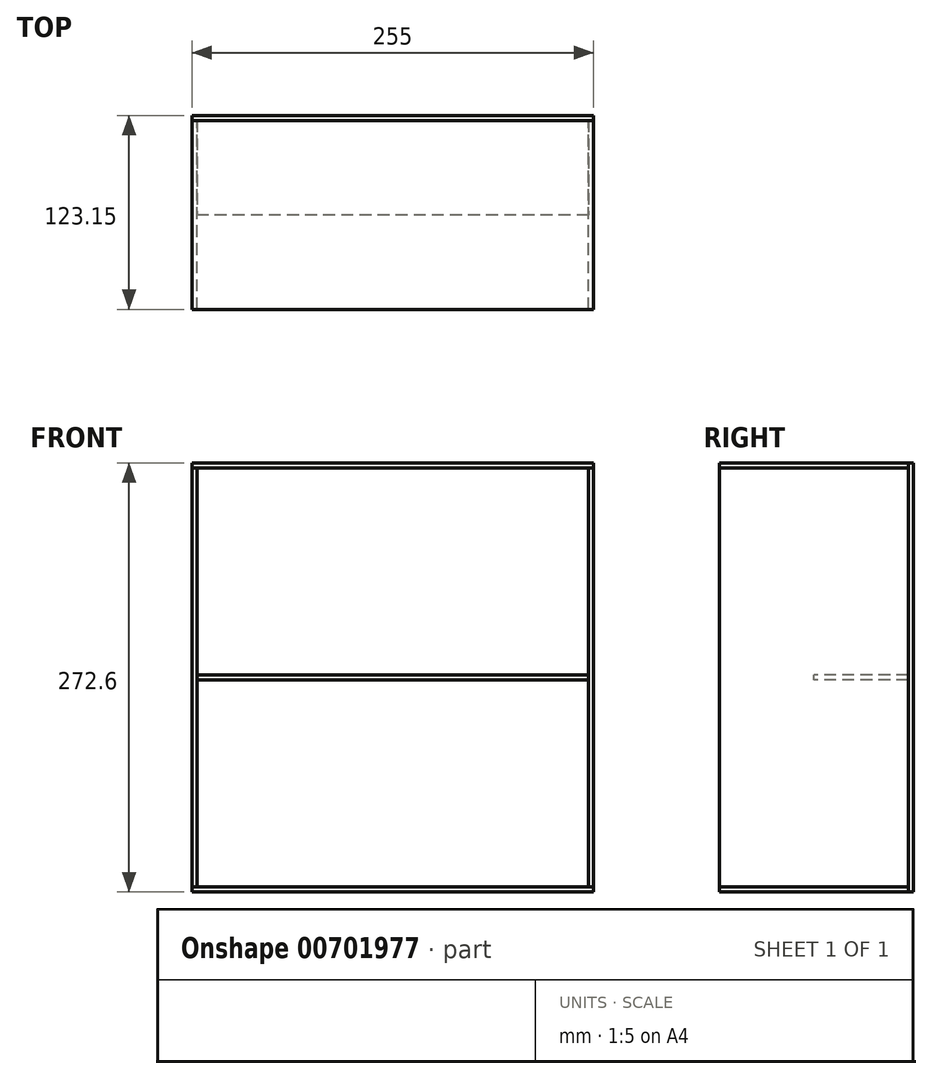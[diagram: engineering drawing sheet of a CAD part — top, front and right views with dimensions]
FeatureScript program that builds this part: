
annotation { "Feature Type Name" : "Feature", "Feature Type Description" : "" }
export const myFeature = defineFeature(function(context is Context, id is Id, definition is map)
    precondition{}
    {
        {
            assignVariable(context, id + "F0", {"name" : "x", "anyValue" : 3.15});
        }
        {
            var Q0;
            Q0=qCreatedBy(makeId("Top.planeOp"),FACE);
            var sketch = newSketch(context, id + "F1", { "sketchPlane" : qUnion([Q0])});
            skLineSegment(sketch, "E0.bottom", {"start": v(0, 0) * mm, "end": v(255, 0) * mm});
            skLineSegment(sketch, "E0.top", {"start": v(0, 120) * mm, "end": v(255, 120) * mm});
            skLineSegment(sketch, "E0.left", {"start": v(0, 0) * mm, "end": v(0, 120) * mm});
            skLineSegment(sketch, "E0.right", {"start": v(255, 0) * mm, "end": v(255, 120) * mm});
            skSolve(sketch);
        }
        {
            var Q0;
            Q0=qSketchRegion(id+"F1",true);
            extrude(context, id + "F2", {"entities" : qUnion([Q0]), "depth" : (getVariable(context, 'x')) * mm, "offsetDistance" : 25 * mm});
        }
        {
            var Q0;
            Q0=makeQuery(id+"F2.opExtrude","SWEPT_FACE",FACE,{"disambiguationData":[OSD([sQuery(id+"F1.wireOp",EDGE,"E0.left")])]});
            var sketch = newSketch(context, id + "F3", { "sketchPlane" : qUnion([Q0])});
            skLineSegment(sketch, "E1.top", {"start": v(0, 269.45) * mm, "end": v(-120, 269.45) * mm});
            skLineSegment(sketch, "E1.left", {"start": v(0, 3.15) * mm, "end": v(0, 269.45) * mm});
            skLineSegment(sketch, "E2", {"start": v(0, 3.15) * mm, "end": v(-120, 3.15) * mm});
            skLineSegment(sketch, "E3", {"start": v(-120, 3.15) * mm, "end": v(-120, 269.45) * mm});
            skSolve(sketch);
        }
        {
            var Q0;
            Q0=qSketchRegion(id+"F3",true);
            extrude(context, id + "F4", {"entities" : qUnion([Q0]), "oppositeDirection" : true, "depth" : (getVariable(context, 'x')) * mm, "offsetDistance" : 25 * mm});
        }
        {
            var Q0;
            Q0=makeQuery(id+"FVTuVMvbx6C6lcW_2.boolean.opBoolean","MERGE",FACE,{"derivedFrom":[makeQuery(id+"F4.opExtrude","SWEPT_FACE",FACE,{"disambiguationData":[OSD([sQuery(id+"F3.wireOp",EDGE,"E1.left")])]}),makeQuery(id+"FVTuVMvbx6C6lcW_2.opExtrude","SWEPT_FACE",FACE,{"disambiguationData":[OSD([sQuery(id+"F9WBSx8lvzqTq6O_2.wireOp",EDGE,"DdJYWYcg-8VXy-0sGO-iMAo-MInbchsGbsPU")])]})]});
            var sketch = newSketch(context, id + "F5", { "sketchPlane" : qUnion([Q0])});
            skLineSegment(sketch, "E4.bottom", {"start": v(3.15, 137.88) * mm, "end": v(251.85, 137.88) * mm});
            skLineSegment(sketch, "E4.top", {"start": v(3.15, 134.73) * mm, "end": v(251.85, 134.73) * mm});
            skLineSegment(sketch, "E4.right", {"start": v(251.85, 137.88) * mm, "end": v(251.85, 134.73) * mm});
            skLineSegment(sketch, "E5", {"start": v(251.85, 3.15) * mm, "end": v(251.85, 134.73) * mm, "construction": true});
            skLineSegment(sketch, "E6", {"start": v(3.15, 134.73) * mm, "end": v(3.15, 137.88) * mm});
            skPoint(sketch, "E7", {"position": v(3.15, 136.3) * mm});
            skSolve(sketch);
        }
        {
            var Q0;
            Q0=qSketchRegion(id+"F5",true);
            var Q1;
            Q1=makeQuery(id+"F4.opExtrude","SWEPT_FACE",FACE,{"disambiguationData":[OSD([sQuery(id+"F3.wireOp",EDGE,"E3")])]});
            extrude(context, id + "F6", {"entities" : qUnion([Q0]), "endBound" : BoundingType.UP_TO_SURFACE, "oppositeDirection" : true, "depth" : 25 * mm, "endBoundEntityFace" : qUnion([Q1]), "offsetDistance" : 25 * mm});
        }
        {
            var Q0;
            Q0=makeQuery(id+"F2.opExtrude","SWEPT_BODY",BODY,{"disambiguationData":[OSD([sQuery(id+"F1.wireOp",EDGE,"E0.bottom"),sQuery(id+"F1.wireOp",EDGE,"E0.top"),sQuery(id+"F1.wireOp",EDGE,"E0.left"),sQuery(id+"F1.wireOp",EDGE,"E0.right")])]});
            transform(context, id + "F7", {"entities" : qUnion([Q0]), "transformType" : TransformType.TRANSLATION_3D, "dx" : 0 * mm, "dy" : 0 * mm, "dz" : (266.3 + 3.15) * mm, "makeCopy" : true});
        }
        {
            var Q0;
            Q0=makeQuery(id+"F4.opExtrude","SWEPT_BODY",BODY,{"disambiguationData":[OSD([sQuery(id+"F3.wireOp",EDGE,"E1.top"),sQuery(id+"F3.wireOp",EDGE,"E1.left"),sQuery(id+"F3.wireOp",EDGE,"E2"),sQuery(id+"F3.wireOp",EDGE,"E3")])]});
            transform(context, id + "F8", {"entities" : qUnion([Q0]), "transformType" : TransformType.TRANSLATION_3D, "dx" : (263.7 + 3.15 - 15) * mm, "dy" : 0 * mm, "dz" : 0 * mm, "makeCopy" : true});
        }
        {
            var Q0;
            Q0=makeQuery(id+"F7.opPattern","COPY",FACE,{"derivedFrom":makeQuery(id+"F2.opExtrude","SWEPT_FACE",FACE,{"disambiguationData":[OSD([sQuery(id+"F1.wireOp",EDGE,"E0.top")])]}),"instanceName":"1"});
            var sketch = newSketch(context, id + "F9", { "sketchPlane" : qUnion([Q0])});
            skLineSegment(sketch, "E8.bottom", {"start": v(-255, 272.6) * mm, "end": v(0, 272.6) * mm});
            skLineSegment(sketch, "E8.top", {"start": v(-255, 0) * mm, "end": v(0, 0) * mm});
            skLineSegment(sketch, "E8.left", {"start": v(-255, 272.6) * mm, "end": v(-255, 0) * mm});
            skLineSegment(sketch, "E8.right", {"start": v(0, 272.6) * mm, "end": v(0, 0) * mm});
            skSolve(sketch);
        }
        {
            var Q0;
            Q0=qSketchRegion(id+"F9",true);
            extrude(context, id + "F10", {"entities" : qUnion([Q0]), "depth" : (getVariable(context, 'x')) * mm, "offsetDistance" : 25 * mm});
        }
        {
            var Q0;
            Q0=makeQuery(id+"F6.opExtrude","SWEPT_FACE",FACE,{"disambiguationData":[OSD([sQuery(id+"F5.wireOp",EDGE,"E4.bottom")])]});
            var sketch = newSketch(context, id + "F11", { "sketchPlane" : qUnion([Q0])});
            skLineSegment(sketch, "E9.bottom", {"start": v(3.15, 60) * mm, "end": v(251.85, 60) * mm});
            skLineSegment(sketch, "E9.top", {"start": v(3.15, 0) * mm, "end": v(251.85, 0) * mm});
            skLineSegment(sketch, "E9.left", {"start": v(3.15, 60) * mm, "end": v(3.15, 0) * mm});
            skLineSegment(sketch, "E9.right", {"start": v(251.85, 60) * mm, "end": v(251.85, 0) * mm});
            skSolve(sketch);
        }
        {
            var Q0;
            Q0=qSketchRegion(id+"F11",true);
            extrude(context, id + "F12", {"entities" : qUnion([Q0]), "operationType" : NewBodyOperationType.REMOVE, "oppositeDirection" : true, "depth" : 25 * mm, "offsetDistance" : 25 * mm});
        }
    });
